# Revit family: Electrical-Teknion-NBAA_Banqs_Sofa_Undermounted_Power-R2019
name_source: partatom
category: Furniture
units: mm (PartAtom-declared; Revit-internal decimal feet)

## family parameters
Always vertical = Yes
Cut with Voids When Loaded = No
OmniClass Number = 23.40.20.00
OmniClass Title = General Furniture and Specialties
Room Calculation Point = No
Shared = Yes
Work Plane-Based = No

## types (2) — shared parameters
Assembly Code = E2020200
Manufacturer = Teknion
Manufacturer Fax = 416.661.4586
Part Number = NBAA
Product Documentation Link = https://www.teknion.com
Product Line = Banqs
Product Page URL = https://www.teknion.com
Series = Soft Seating
Sustainability Data = https://www.teknion.com
URL = www.teknion.com
Unit Weight URL = http://www.teknion.com
Warranty = http://www.teknion.com

## per-type parameters (varying)
| type | Description | Electrical Finishes | Model |
| White Finishes | Sofa Undermounted Power, 1 Power, 1 USB-A and 1 USB-C White | Plastic - Teknion - White | NBAAW |
| Black Finishes | Sofa Undermounted Power, 1 Power, 1 USB-A and 1 USB-C Black | Plastic - Teknion - E - Ebony | NBAAB |

## geometry (parser evidence)
native form markers: Sweep x2
no freeform markers — native parametric forms only
